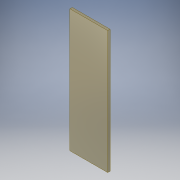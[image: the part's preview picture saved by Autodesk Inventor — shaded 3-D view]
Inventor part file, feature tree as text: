
AUTODESK INVENTOR PART (.ipt)
format: ipt  version: 2019.4 (Build 234330000, 330)  size: 98,816 bytes
history: native  units: mm
features: extrude x1, sketch x1
ambient origin geometry x8: Origin, YZ Plane, XZ Plane, XY Plane, X Axis, Y Axis, Z Axis, Center Point
bodies: Solid1 (feature_tree)
feature tree (2):
  extrude  "Extrusion1"  Depth=9.165mm
  sketch  "Sketch1"  dims[d0=18.33mm d1=9.165mm d2=26.0mm d3=8.0mm d4=0.5mm d5=0.0mm]
